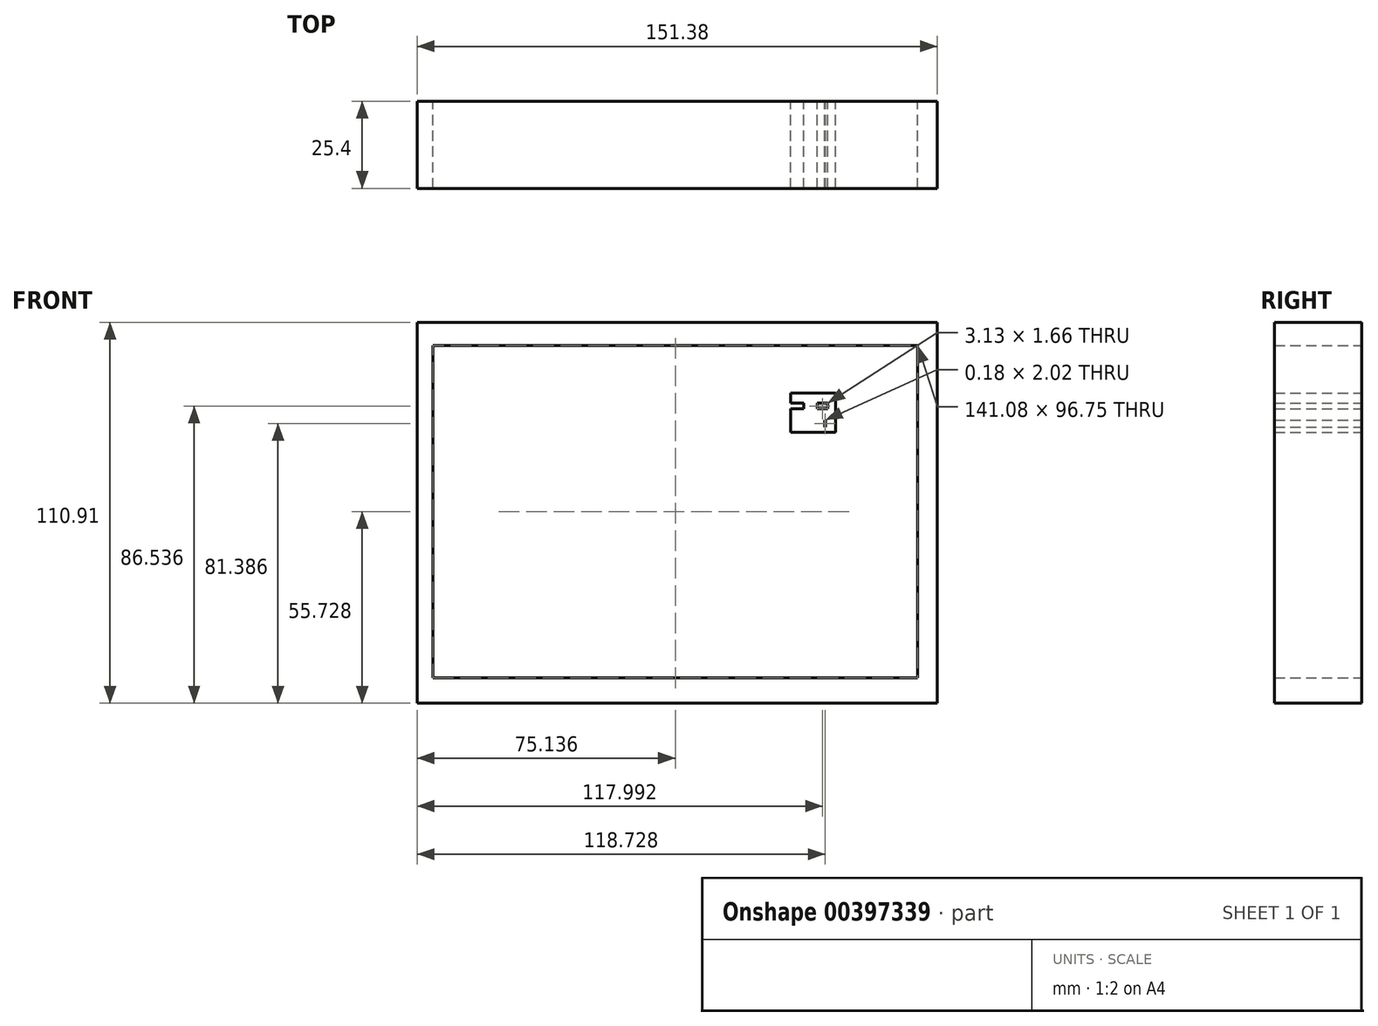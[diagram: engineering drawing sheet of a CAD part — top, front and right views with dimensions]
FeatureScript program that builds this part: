
annotation { "Feature Type Name" : "Feature", "Feature Type Description" : "" }
export const myFeature = defineFeature(function(context is Context, id is Id, definition is map)
    precondition{}
    {
        {
            var Q0;
            Q0=qCreatedBy(makeId("Front.planeOp"),FACE);
            var sketch = newSketch(context, id + "F0", { "sketchPlane" : qUnion([Q0])});
            skLineSegment(sketch, "E0.bottom", {"start": v(-75.78, -55.36) * mm, "end": v(75.6, -55.36) * mm});
            skLineSegment(sketch, "E0.top", {"start": v(-75.78, 55.55) * mm, "end": v(75.6, 55.55) * mm});
            skLineSegment(sketch, "E0.left", {"start": v(-75.78, -55.36) * mm, "end": v(-75.78, 55.55) * mm});
            skLineSegment(sketch, "E0.right", {"start": v(75.6, -55.36) * mm, "end": v(75.6, 55.55) * mm});
            skLineSegment(sketch, "E1.bottom", {"start": v(-71.18, 48.74) * mm, "end": v(69.9, 48.74) * mm});
            skLineSegment(sketch, "E1.top", {"start": v(-71.18, -48) * mm, "end": v(69.9, -48) * mm});
            skLineSegment(sketch, "E1.left", {"start": v(-71.18, 48.74) * mm, "end": v(-71.18, -48) * mm});
            skLineSegment(sketch, "E1.right", {"start": v(69.9, 48.74) * mm, "end": v(69.9, -48) * mm});
            skSolve(sketch);
        }
        {
            var Q0;
            Q0=makeQuery(id+"F0.imprint","IMPRINT",FACE,{"disambiguationData":[TD([[makeQuery(id+"F0.imprint","IMPRINT",EDGE,{"derivedFrom":sQuery(id+"F0.wireOp",EDGE,"E0.bottom")}),1.0]])]});
            extrude(context, id + "F1", {"entities" : qUnion([Q0]), "depth" : 25.4 * mm});
        }
        {
            var Q0;
            Q0=qCreatedBy(makeId("Front.planeOp"),FACE);
            var sketch = newSketch(context, id + "F2", { "sketchPlane" : qUnion([Q0])});
            skLineSegment(sketch, "E2.bottom", {"start": v(45.98, 23.54) * mm, "end": v(32.92, 23.54) * mm});
            skLineSegment(sketch, "E2.top", {"start": v(45.98, 34.95) * mm, "end": v(32.92, 34.95) * mm});
            skLineSegment(sketch, "E2.left", {"start": v(45.98, 23.54) * mm, "end": v(45.98, 34.95) * mm});
            skLineSegment(sketch, "E2.right", {"start": v(32.92, 23.54) * mm, "end": v(32.92, 34.95) * mm});
            skLineSegment(sketch, "E3.bottom", {"start": v(43.78, 30.35) * mm, "end": v(40.65, 30.35) * mm});
            skLineSegment(sketch, "E3.top", {"start": v(43.78, 32) * mm, "end": v(40.65, 32) * mm});
            skLineSegment(sketch, "E3.left", {"start": v(43.78, 30.35) * mm, "end": v(43.78, 32) * mm});
            skLineSegment(sketch, "E3.right", {"start": v(40.65, 30.35) * mm, "end": v(40.65, 32) * mm});
            skLineSegment(sketch, "E4.bottom", {"start": v(36.79, 30.35) * mm, "end": v(32.92, 30.35) * mm});
            skLineSegment(sketch, "E4.top", {"start": v(36.79, 32) * mm, "end": v(32.92, 32) * mm});
            skLineSegment(sketch, "E4.left", {"start": v(36.79, 30.35) * mm, "end": v(36.79, 32) * mm});
            skLineSegment(sketch, "E4.right", {"start": v(32.92, 30.35) * mm, "end": v(32.92, 32) * mm});
            skLineSegment(sketch, "E5.bottom", {"start": v(43.04, 25.01) * mm, "end": v(42.86, 25.01) * mm});
            skLineSegment(sketch, "E5.top", {"start": v(43.04, 27.04) * mm, "end": v(42.86, 27.04) * mm});
            skLineSegment(sketch, "E5.left", {"start": v(43.04, 25.01) * mm, "end": v(43.04, 27.04) * mm});
            skLineSegment(sketch, "E5.right", {"start": v(42.86, 25.01) * mm, "end": v(42.86, 27.04) * mm});
            skLineSegment(sketch, "E6.bottom", {"start": v(42.86, 27.04) * mm, "end": v(36.97, 27.04) * mm});
            skLineSegment(sketch, "E6.top", {"start": v(42.86, 27.04) * mm, "end": v(36.97, 27.04) * mm});
            skLineSegment(sketch, "E6.left", {"start": v(42.86, 27.04) * mm, "end": v(42.86, 27.04) * mm});
            skLineSegment(sketch, "E6.right", {"start": v(36.97, 27.04) * mm, "end": v(36.97, 27.04) * mm});
            skLineSegment(sketch, "E7.bottom", {"start": v(36.97, 25.2) * mm, "end": v(36.97, 25.2) * mm});
            skLineSegment(sketch, "E7.left", {"start": v(36.97, 25.2) * mm, "end": v(36.97, 27.04) * mm});
            skLineSegment(sketch, "E7.right", {"start": v(36.97, 25.2) * mm, "end": v(36.97, 27.04) * mm});
            skSolve(sketch);
        }
        {
            var Q0;
            {var subQ5=sQuery(id+"F2.wireOp",EDGE,"E2.bottom");Q0=makeQuery(id+"F2.imprint","IMPRINT",FACE,{"disambiguationData":[TD([[makeQuery(id+"F2.imprint","IMPRINT",EDGE,{"derivedFrom":subQ5}),-1.0]])]});}
            extrude(context, id + "F3", {"entities" : qUnion([Q0]), "depth" : 25.4 * mm});
        }
    });
